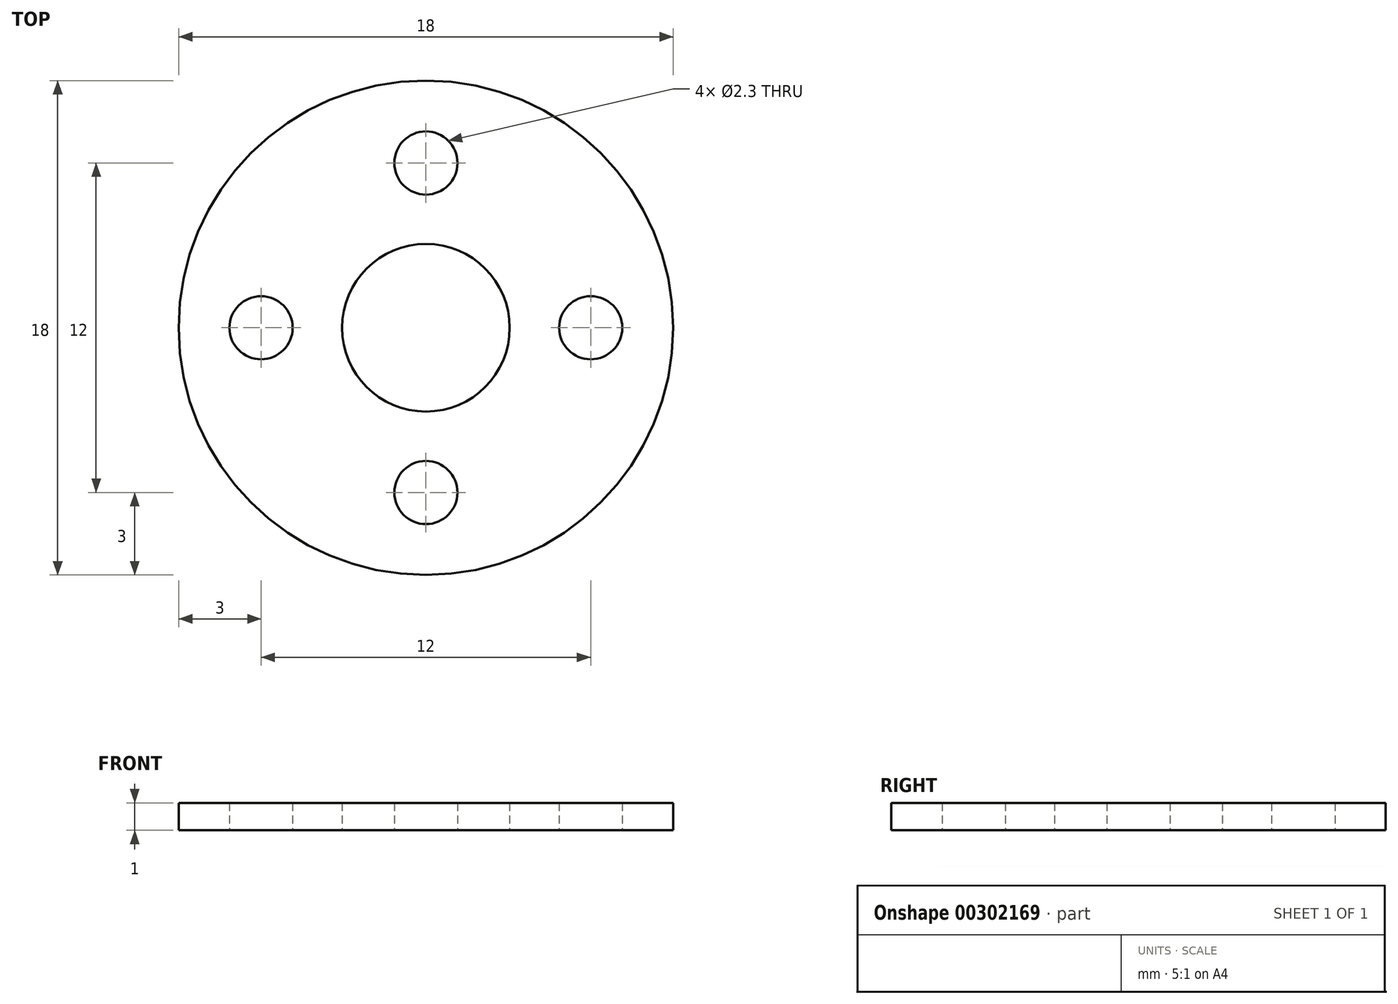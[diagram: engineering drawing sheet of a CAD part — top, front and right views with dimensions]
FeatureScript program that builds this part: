
annotation { "Feature Type Name" : "Feature", "Feature Type Description" : "" }
export const myFeature = defineFeature(function(context is Context, id is Id, definition is map)
    precondition{}
    {
        {
            var Q0;
            Q0=qCreatedBy(makeId("Top.planeOp"),FACE);
            var sketch = newSketch(context, id + "F0", { "sketchPlane" : qUnion([Q0])});
            skCircle(sketch, "E0.MirrorC", {"center": v(0, 6) * mm, "radius": 1.15 * mm});
            skCircle(sketch, "E1.MirrorC", {"center": v(-6, 0) * mm, "radius": 1.15 * mm});
            skCircle(sketch, "E2.MirrorC", {"center": v(0, -6) * mm, "radius": 1.15 * mm});
            skCircle(sketch, "E3.MirrorC", {"center": v(6, 0) * mm, "radius": 1.15 * mm});
            skCircle(sketch, "E4.MirrorC", {"center": v(0, 0) * mm, "radius": 3.05 * mm});
            skCircle(sketch, "E5", {"center": v(0, 0) * mm, "radius": 6 * mm, "construction": true});
            skCircle(sketch, "E6", {"center": v(0, 0) * mm, "radius": 9 * mm});
            skSolve(sketch);
        }
        {
            var Q0;
            Q0 = qSketchRegion(id + "F0", true);
            var Q1;
            Q1 = qConstructionFilter(qBodyType(qCreatedBy(id + "F0" ,EDGE), BodyType.WIRE), ConstructionObject.NO);
            extrude(context, id + "F1", {"entities" : qUnion([Q0]), "surfaceEntities" : qUnion([Q1]), "depth" : 1 * mm});
        }
    });
